FCSTD DOCUMENT  (FreeCAD 2023.131R14555 (Git shallow))
Label: dimensions
License: Creative Commons Attribution-NoDerivatives
LicenseURL: http://creativecommons.org/licenses/by-nd/4.0/
objects: Image::ImagePlane×1, Sketcher::SketchObject×1
note: 2 computed .brp shape members not serialized (recipe doc carries the construction recipe); baked Part::Feature solids carry a one-line shape summary decoded from their .brp

FEATURE [Image::ImagePlane] ImagePlane
  Placement = pos=(0,0,0) rot=(0,0,1;0.022689rad)
  TreeRank = 1
  XSize = 23.5775
  YSize = 51.1203
FEATURE [Sketcher::SketchObject] Sketch
  ArcFitTolerance = 1e-06
  ExternalBSplineMaxDegree = 5
  ExternalBSplineTolerance = 0.0001
  FixShape = 1
  FullyConstrained = false
  InternalTolerance = 1e-06
  InvalidShape = false
  MakeInternals = true
  TreeRank = 2
  ValidateShape = false
  sketch-geometry (18):
    g0: LineSegment StartX=-8.1397 StartY=15.6042 StartZ=0 EndX=8.38964 EndY=15.6042 EndZ=0
    g1: LineSegment StartX=8.38964 StartY=15.6042 StartZ=0 EndX=8.38964 EndY=-17.2756 EndZ=0
    g2: LineSegment StartX=8.38964 StartY=-17.2756 StartZ=0 EndX=-8.1397 EndY=-17.2756 EndZ=0
    g3: LineSegment StartX=-8.1397 StartY=-17.2756 StartZ=0 EndX=-8.1397 EndY=15.6042 EndZ=0
    g4: Circle CenterX=-1.75 CenterY=12.34 CenterZ=0 NormalX=0 NormalY=0 NormalZ=1 AngleXU=0 Radius=0.506218
    g5: Circle CenterX=1.75 CenterY=12.34 CenterZ=0 NormalX=0 NormalY=0 NormalZ=1 AngleXU=0 Radius=0.467654
    g6: Circle CenterX=-1.27 CenterY=13.94 CenterZ=0 NormalX=0 NormalY=0 NormalZ=1 AngleXU=0 Radius=0.472902
    g7: Circle CenterX=1.27 CenterY=13.94 CenterZ=0 NormalX=0 NormalY=0 NormalZ=1 AngleXU=0 Radius=0.459001
    g8: Circle CenterX=-3.5 CenterY=-13.77 CenterZ=0 NormalX=0 NormalY=0 NormalZ=1 AngleXU=0 Radius=0.55058
    g9: Circle CenterX=-2.701e-12 CenterY=-13.77 CenterZ=0 NormalX=0 NormalY=0 NormalZ=1 AngleXU=0 Radius=0.55058
    g10: Circle CenterX=3.5 CenterY=-13.77 CenterZ=0 NormalX=0 NormalY=0 NormalZ=1 AngleXU=0 Radius=0.55058
    g11: Circle CenterX=-5.08 CenterY=-15.42 CenterZ=0 NormalX=0 NormalY=0 NormalZ=1 AngleXU=0 Radius=1.04513
    g12: Circle CenterX=-2.701e-12 CenterY=-15.42 CenterZ=0 NormalX=0 NormalY=0 NormalZ=1 AngleXU=0 Radius=1.04513
    g13: Circle CenterX=5.08 CenterY=-15.42 CenterZ=0 NormalX=0 NormalY=0 NormalZ=1 AngleXU=0 Radius=1.04513
    g14: LineSegment [constr] StartX=-1.27 StartY=13.94 StartZ=0 EndX=1.27 EndY=13.94 EndZ=0
    g15: GeomPoint [constr] X=-2.701e-12 Y=13.94 Z=0
    g16: LineSegment [constr] StartX=-1.75 StartY=12.34 StartZ=0 EndX=1.75 EndY=12.34 EndZ=0
    g17: GeomPoint [constr] X=-2.701e-12 Y=12.34 Z=0
  constraints (39):
    c: Coincident(g0,g1)
    c: Coincident(g1,g2)
    c: Coincident(g2,g3)
    c: Coincident(g3,g0)
    c: Horizontal(g0)
    c: Horizontal(g2)
    c: Vertical(g1)
    c: Vertical(g3)
    c: DistanceX(g6,g7) = 2.54
    c: Horizontal(g7,g6)
    c: Horizontal(g4,g5)
    c: DistanceX(g4,g5) = 3.5
    c: Horizontal(g8,g9)
    c: Horizontal(g12,g11)
    c: Equal(g13,g12)
    c: Equal(g12,g11)
    c: Equal(g10,g9)
    c: Equal(g9,g8)
    c: DistanceX(g8,g9) = 3.5
    c: Symmetric(g8,g10,g9)
    c: Symmetric(g11,g13,g12)
    c: DistanceX(g11,g12) = 5.08
    c: Coincident(g14,g6)
    c: Coincident(g7,g14)
    c: Symmetric(g6,g7,g15)
    c: Coincident(g16,g4)
    c: Coincident(g16,g5)
    c: Symmetric(g4,g5,g17)
    c: Vertical(g15,g17)
    c: Vertical(g17,g9)
    c: Vertical(g12,g9)
    c: PointOnObject(g15,g-2)
    c: DistanceY(g12,g9) = 1.65
    c: DistanceY(g17,g15) = 1.6
    c: DistanceY(g9,g17) = 26.11
    c: DistanceY(g9,g-1) = 13.77
    c: DistanceY(g12,g-1) = 15.42
    c: DistanceY(g-1,g17) = 12.34
    c: DistanceY(g-1,g7) = 13.94
